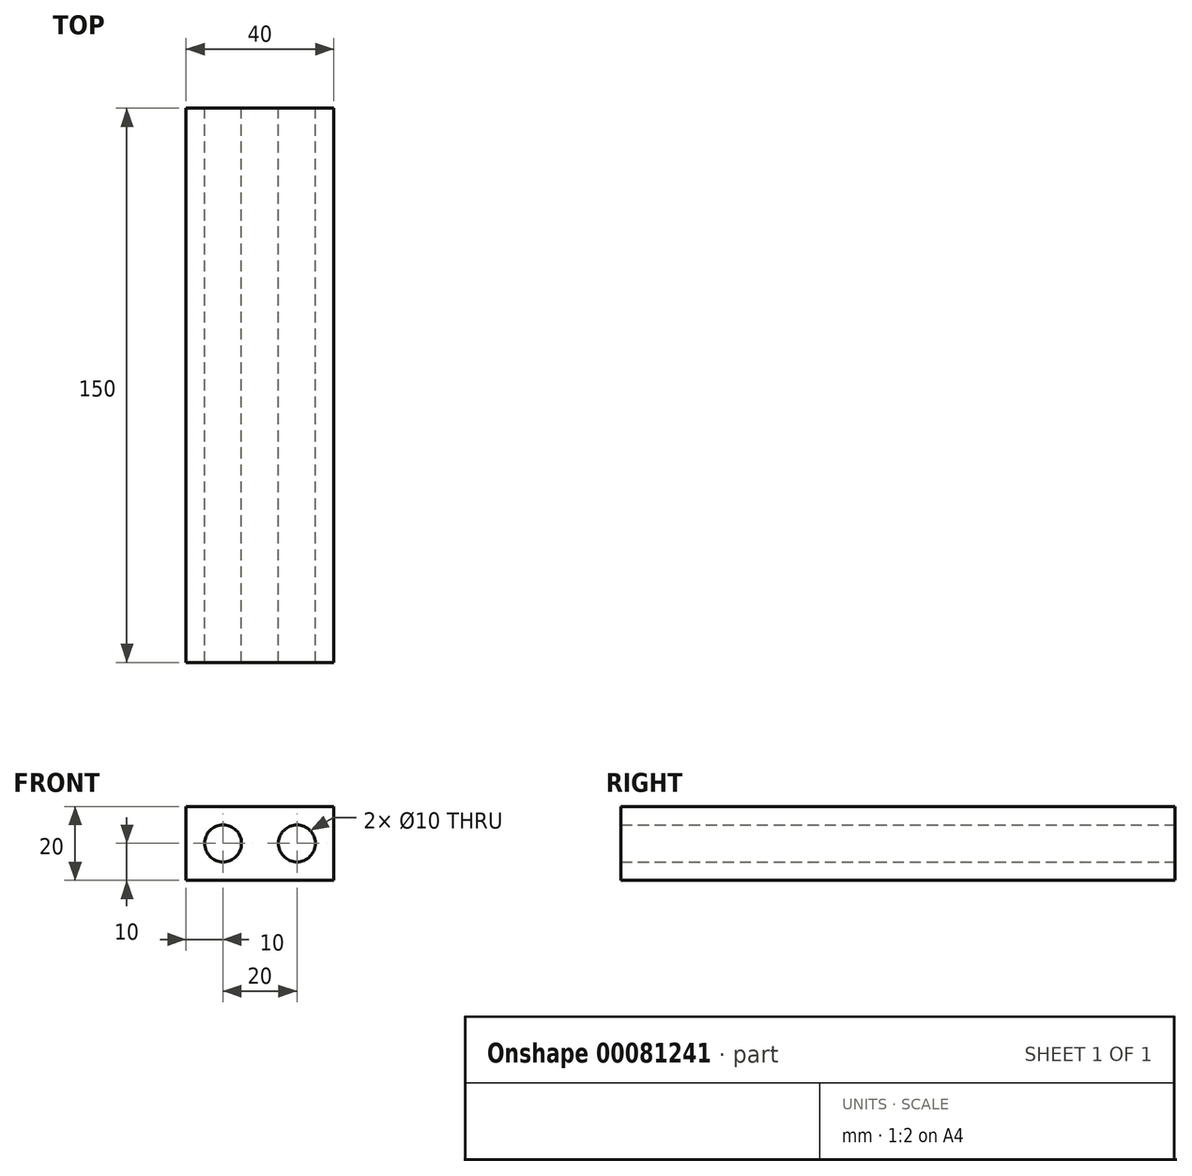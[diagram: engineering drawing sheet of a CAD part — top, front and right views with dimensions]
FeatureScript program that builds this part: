
annotation { "Feature Type Name" : "Feature", "Feature Type Description" : "" }
export const myFeature = defineFeature(function(context is Context, id is Id, definition is map)
    precondition{}
    {
        {
            var Q0;
            Q0=qCreatedBy(makeId("Front.planeOp"),FACE);
            var sketch = newSketch(context, id + "F0", { "sketchPlane" : qUnion([Q0])});
            skLineSegment(sketch, "E0.bottom", {"start": v(10, -10) * mm, "end": v(-10, -10) * mm});
            skLineSegment(sketch, "E0.top", {"start": v(10, 10) * mm, "end": v(-10, 10) * mm});
            skLineSegment(sketch, "E0.right", {"start": v(-10, -10) * mm, "end": v(-10, 10) * mm});
            skPoint(sketch, "E0.middle", {"position": v(0, 0) * mm});
            skCircle(sketch, "E1", {"center": v(0, 0) * mm, "radius": 5 * mm});
            skPoint(sketch, "E2.endSnap0", {"position": v(10, 0) * mm});
            skLineSegment(sketch, "E3.MirrorCS", {"start": v(10, -10) * mm, "end": v(30, -10) * mm});
            skLineSegment(sketch, "E4.MirrorCS", {"start": v(10, 10) * mm, "end": v(30, 10) * mm});
            skLineSegment(sketch, "E5.MirrorCS", {"start": v(30, -10) * mm, "end": v(30, 10) * mm});
            skCircle(sketch, "E6.MirrorC", {"center": v(20, 0) * mm, "radius": 5 * mm});
            skPoint(sketch, "E7.orphan", {"position": v(10, -61.67) * mm});
            skPoint(sketch, "E2.start.orphan", {"position": v(10, 43.8) * mm});
            skSolve(sketch);
        }
        {
            var Q0;
            Q0=makeQuery(id+"F0.imprint","IMPRINT",FACE,{"disambiguationData":[TD([[makeQuery(id+"F0.imprint","IMPRINT",EDGE,{"derivedFrom":sQuery(id+"F0.wireOp",EDGE,"E0.bottom")}),-1.0]])]});
            extrude(context, id + "F1", {"entities" : qUnion([Q0]), "depth" : 75 * mm, "hasSecondDirection" : true, "secondDirectionOppositeDirection" : true, "secondDirectionDepth" : 75 * mm});
        }
    });
